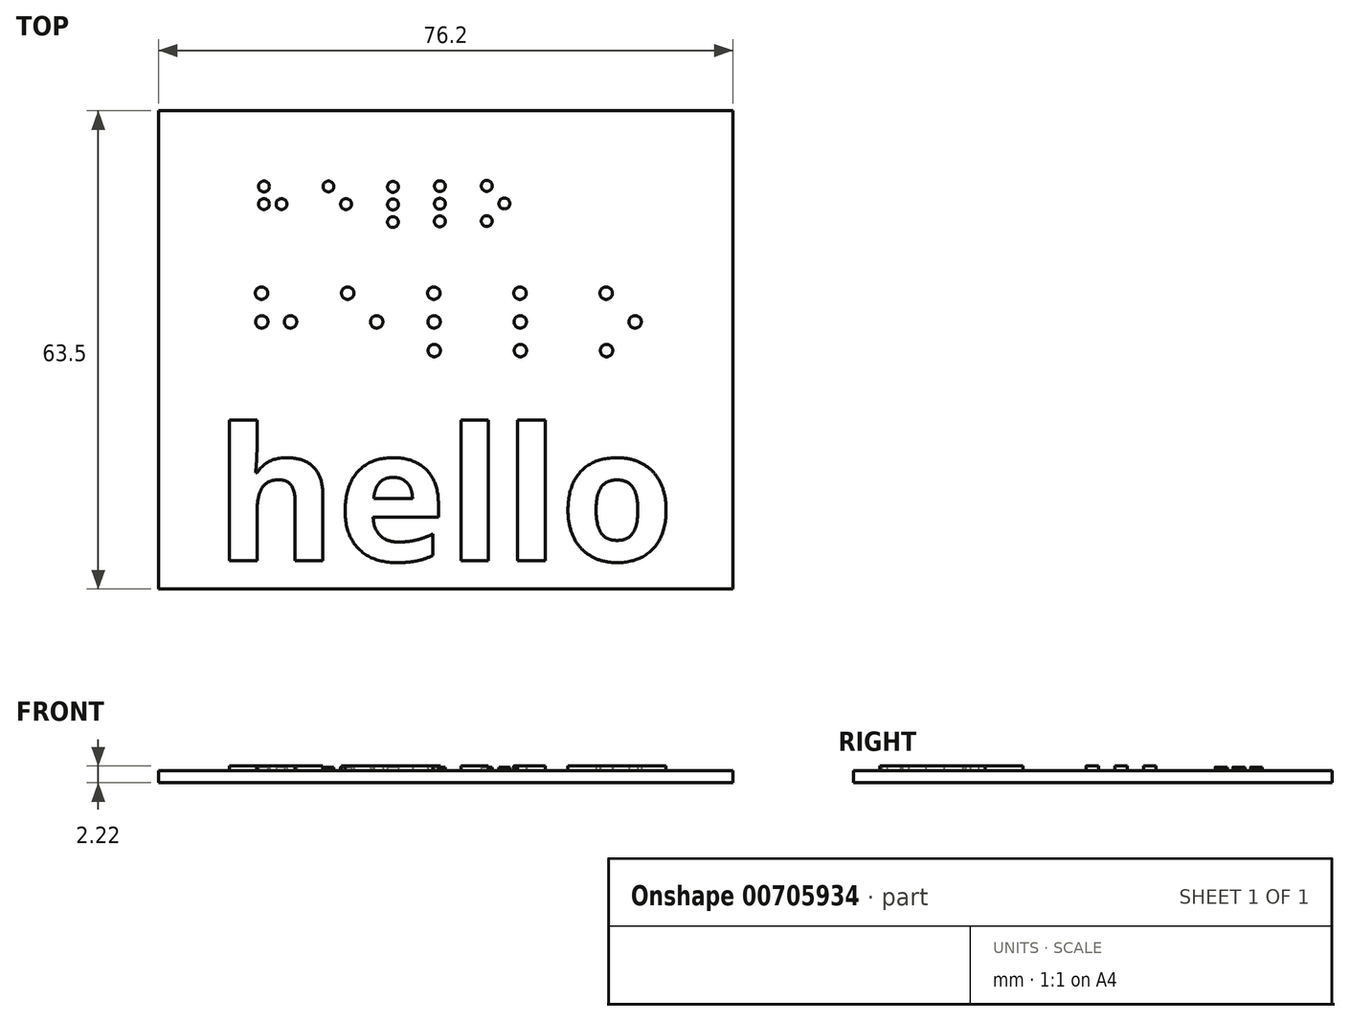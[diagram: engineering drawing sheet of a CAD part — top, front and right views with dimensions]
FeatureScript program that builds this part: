
annotation { "Feature Type Name" : "Feature", "Feature Type Description" : "" }
export const myFeature = defineFeature(function(context is Context, id is Id, definition is map)
    precondition{}
    {
        {
            var Q0;
            Q0=qCreatedBy(makeId("Top.planeOp"),FACE);
            var sketch = newSketch(context, id + "F0", { "sketchPlane" : qUnion([Q0])});
            skLineSegment(sketch, "E0.bottom", {"start": v(2.28, 0) * mm, "end": v(78.48, 0) * mm});
            skLineSegment(sketch, "E0.top", {"start": v(2.28, 63.5) * mm, "end": v(78.48, 63.5) * mm});
            skLineSegment(sketch, "E0.left", {"start": v(2.28, 0) * mm, "end": v(2.28, 63.5) * mm});
            skLineSegment(sketch, "E0.right", {"start": v(78.48, 0) * mm, "end": v(78.48, 63.5) * mm});
            skSolve(sketch);
        }
        {
            var Q0;
            Q0=makeQuery(id+"F0.imprint","IMPRINT",FACE,{"disambiguationData":[TD([[makeQuery(id+"F0.imprint","IMPRINT",EDGE,{"derivedFrom":sQuery(id+"F0.wireOp",EDGE,"E0.bottom")}),1.0]])]});
            extrude(context, id + "F1", {"entities" : qUnion([Q0]), "depth" : 1.59 * mm, "offsetDistance" : 25.4 * mm});
        }
        {
            var Q0;
            Q0=makeQuery(id+"F1.opExtrude","CAP_FACE",FACE,{"disambiguationData":[OSD([sQuery(id+"F0.wireOp",EDGE,"E0.bottom"),sQuery(id+"F0.wireOp",EDGE,"E0.top"),sQuery(id+"F0.wireOp",EDGE,"E0.left"),sQuery(id+"F0.wireOp",EDGE,"E0.right")])],"isStart":false});
            var sketch = newSketch(context, id + "F2", { "sketchPlane" : qUnion([Q0])});
            skCircle(sketch, "E1", {"center": v(16.26, 53.45) * mm, "radius": 0.72 * mm});
            skLineSegment(sketch, "E2.direction1", {"start": v(16.26, 53.45) * mm, "end": v(18.6, 53.45) * mm, "construction": true});
            skCircle(sketch, "E3.1.0.0", {"center": v(16.26, 51.11) * mm, "radius": 0.72 * mm});
            skCircle(sketch, "E3.1.0.1", {"center": v(18.6, 51.11) * mm, "radius": 0.72 * mm});
            skLineSegment(sketch, "E3.direction1", {"start": v(16.26, 53.45) * mm, "end": v(16.26, 51.11) * mm, "construction": true});
            skCircle(sketch, "E4", {"center": v(24.82, 53.45) * mm, "radius": 0.72 * mm});
            skCircle(sketch, "E5.1.0.1", {"center": v(27.15, 51.11) * mm, "radius": 0.72 * mm});
            skCircle(sketch, "E6", {"center": v(33.38, 53.4) * mm, "radius": 0.72 * mm});
            skCircle(sketch, "E7.1.0.0", {"center": v(33.38, 51.06) * mm, "radius": 0.72 * mm});
            skCircle(sketch, "E7.2.0.0", {"center": v(33.37, 48.73) * mm, "radius": 0.72 * mm});
            skCircle(sketch, "E8", {"center": v(39.6, 53.5) * mm, "radius": 0.72 * mm});
            skCircle(sketch, "E9.1.0.0", {"center": v(39.6, 51.16) * mm, "radius": 0.72 * mm});
            skCircle(sketch, "E9.2.0.0", {"center": v(39.6, 48.82) * mm, "radius": 0.72 * mm});
            skCircle(sketch, "E10", {"center": v(45.83, 53.53) * mm, "radius": 0.72 * mm});
            skCircle(sketch, "E11.1.0.1", {"center": v(48.16, 51.2) * mm, "radius": 0.72 * mm});
            skCircle(sketch, "E11.2.0.0", {"center": v(45.82, 48.86) * mm, "radius": 0.72 * mm});
            skPoint(sketch, "E3.2.0.0.center.orphan", {"position": v(16.25, 48.78) * mm});
            skPoint(sketch, "E5.1.0.0.center.orphan", {"position": v(24.82, 51.11) * mm});
            skPoint(sketch, "E5.2.0.0.center.orphan", {"position": v(24.81, 48.78) * mm});
            skPoint(sketch, "E12.1.0.0.center.orphan", {"position": v(27.16, 53.45) * mm});
            skPoint(sketch, "E13.1.0.0.center.orphan", {"position": v(35.72, 53.4) * mm});
            skPoint(sketch, "E7.1.0.1.center.orphan", {"position": v(35.71, 51.06) * mm});
            skPoint(sketch, "E7.2.0.1.center.orphan", {"position": v(35.7, 48.73) * mm});
            skPoint(sketch, "E14.1.0.0.center.orphan", {"position": v(41.94, 53.5) * mm});
            skPoint(sketch, "E9.1.0.1.center.orphan", {"position": v(41.94, 51.16) * mm});
            skPoint(sketch, "E9.2.0.1.center.orphan", {"position": v(41.93, 48.82) * mm});
            skPoint(sketch, "E11.1.0.0.center.orphan", {"position": v(45.82, 51.2) * mm});
            skPoint(sketch, "E11.2.0.1.center.orphan", {"position": v(48.15, 48.86) * mm});
            skPoint(sketch, "E15.1.0.0.center.orphan", {"position": v(48.16, 53.53) * mm});
            skPoint(sketch, "E16.center.orphan", {"position": v(52.05, 53.48) * mm});
            skPoint(sketch, "E17.1.0.0.center.orphan", {"position": v(52.05, 51.14) * mm});
            skPoint(sketch, "E17.1.0.1.center.orphan", {"position": v(54.38, 51.14) * mm});
            skPoint(sketch, "E18.1.0.0.center.orphan", {"position": v(54.39, 53.48) * mm});
            skPoint(sketch, "E17.2.0.0.center.orphan", {"position": v(52.04, 48.8) * mm});
            skPoint(sketch, "E17.2.0.1.center.orphan", {"position": v(54.38, 48.8) * mm});
            skPoint(sketch, "E19.orphan", {"position": v(52.04, 48.05) * mm});
            skPoint(sketch, "E20.start.orphan", {"position": v(27.15, 48.78) * mm});
            skPoint(sketch, "E21.start.orphan", {"position": v(16.25, 48.05) * mm});
            skSolve(sketch);
        }
        {
            var Q0;
            Q0=makeQuery(id+"F2.imprint","IMPRINT",FACE,{"disambiguationData":[TD([[makeQuery(id+"F2.imprint","IMPRINT",EDGE,{"derivedFrom":sQuery(id+"F2.wireOp",EDGE,"E3.1.0.0")}),1.0]])]});
            var Q1;
            Q1=makeQuery(id+"F2.imprint","IMPRINT",FACE,{"disambiguationData":[TD([[makeQuery(id+"F2.imprint","IMPRINT",EDGE,{"derivedFrom":sQuery(id+"F2.wireOp",EDGE,"E3.1.0.1")}),1.0]])]});
            var Q2;
            Q2=makeQuery(id+"F2.imprint","IMPRINT",FACE,{"disambiguationData":[TD([[makeQuery(id+"F2.imprint","IMPRINT",EDGE,{"derivedFrom":sQuery(id+"F2.wireOp",EDGE,"E1")}),1.0]])]});
            var Q3;
            Q3=makeQuery(id+"F2.imprint","IMPRINT",FACE,{"disambiguationData":[TD([[makeQuery(id+"F2.imprint","IMPRINT",EDGE,{"derivedFrom":sQuery(id+"F2.wireOp",EDGE,"E4")}),1.0]])]});
            var Q4;
            Q4=makeQuery(id+"F2.imprint","IMPRINT",FACE,{"disambiguationData":[TD([[makeQuery(id+"F2.imprint","IMPRINT",EDGE,{"derivedFrom":sQuery(id+"F2.wireOp",EDGE,"E5.1.0.1")}),1.0]])]});
            var Q5;
            Q5=makeQuery(id+"F2.imprint","IMPRINT",FACE,{"disambiguationData":[TD([[makeQuery(id+"F2.imprint","IMPRINT",EDGE,{"derivedFrom":sQuery(id+"F2.wireOp",EDGE,"E7.2.0.0")}),1.0]])]});
            var Q6;
            Q6=makeQuery(id+"F2.imprint","IMPRINT",FACE,{"disambiguationData":[TD([[makeQuery(id+"F2.imprint","IMPRINT",EDGE,{"derivedFrom":sQuery(id+"F2.wireOp",EDGE,"E7.1.0.0")}),1.0]])]});
            var Q7;
            Q7=makeQuery(id+"F2.imprint","IMPRINT",FACE,{"disambiguationData":[TD([[makeQuery(id+"F2.imprint","IMPRINT",EDGE,{"derivedFrom":sQuery(id+"F2.wireOp",EDGE,"E6")}),1.0]])]});
            var Q8;
            Q8=makeQuery(id+"F2.imprint","IMPRINT",FACE,{"disambiguationData":[TD([[makeQuery(id+"F2.imprint","IMPRINT",EDGE,{"derivedFrom":sQuery(id+"F2.wireOp",EDGE,"E9.2.0.0")}),1.0]])]});
            var Q9;
            Q9=makeQuery(id+"F2.imprint","IMPRINT",FACE,{"disambiguationData":[TD([[makeQuery(id+"F2.imprint","IMPRINT",EDGE,{"derivedFrom":sQuery(id+"F2.wireOp",EDGE,"E9.1.0.0")}),1.0]])]});
            var Q10;
            Q10=makeQuery(id+"F2.imprint","IMPRINT",FACE,{"disambiguationData":[TD([[makeQuery(id+"F2.imprint","IMPRINT",EDGE,{"derivedFrom":sQuery(id+"F2.wireOp",EDGE,"E8")}),1.0]])]});
            var Q11;
            Q11=makeQuery(id+"F2.imprint","IMPRINT",FACE,{"disambiguationData":[TD([[makeQuery(id+"F2.imprint","IMPRINT",EDGE,{"derivedFrom":sQuery(id+"F2.wireOp",EDGE,"E11.2.0.0")}),1.0]])]});
            var Q12;
            Q12=makeQuery(id+"F2.imprint","IMPRINT",FACE,{"disambiguationData":[TD([[makeQuery(id+"F2.imprint","IMPRINT",EDGE,{"derivedFrom":sQuery(id+"F2.wireOp",EDGE,"E11.1.0.1")}),1.0]])]});
            var Q13;
            Q13=makeQuery(id+"F2.imprint","IMPRINT",FACE,{"disambiguationData":[TD([[makeQuery(id+"F2.imprint","IMPRINT",EDGE,{"derivedFrom":sQuery(id+"F2.wireOp",EDGE,"E10")}),1.0]])]});
            extrude(context, id + "F3", {"entities" : qUnion([Q0, Q1, Q2, Q3, Q4, Q5, Q6, Q7, Q8, Q9, Q10, Q11, Q12, Q13]), "operationType" : NewBodyOperationType.ADD, "depth" : 0.48 * mm, "offsetDistance" : 25.4 * mm});
        }
        {
            var Q0;
            Q0=makeQuery(id+"F1.opExtrude","CAP_FACE",FACE,{"disambiguationData":[OSD([sQuery(id+"F0.wireOp",EDGE,"E0.bottom"),sQuery(id+"F0.wireOp",EDGE,"E0.top"),sQuery(id+"F0.wireOp",EDGE,"E0.left"),sQuery(id+"F0.wireOp",EDGE,"E0.right")])],"isStart":false});
            var sketch = newSketch(context, id + "F4", { "sketchPlane" : qUnion([Q0])});
            skCircle(sketch, "E22", {"center": v(15.94, 39.3) * mm, "radius": 0.83 * mm});
            skCircle(sketch, "E23.1.0.0", {"center": v(15.97, 35.48) * mm, "radius": 0.83 * mm});
            skCircle(sketch, "E23.1.0.1", {"center": v(19.78, 35.48) * mm, "radius": 0.83 * mm});
            skCircle(sketch, "E24", {"center": v(27.37, 39.3) * mm, "radius": 0.83 * mm});
            skCircle(sketch, "E25.1.0.1", {"center": v(31.2, 35.48) * mm, "radius": 0.83 * mm});
            skCircle(sketch, "E26", {"center": v(38.8, 39.3) * mm, "radius": 0.83 * mm});
            skCircle(sketch, "E27.1.0.0", {"center": v(38.83, 35.48) * mm, "radius": 0.83 * mm});
            skCircle(sketch, "E27.2.0.0", {"center": v(38.86, 31.67) * mm, "radius": 0.83 * mm});
            skCircle(sketch, "E28", {"center": v(50.23, 39.3) * mm, "radius": 0.83 * mm});
            skCircle(sketch, "E29.1.0.0", {"center": v(50.26, 35.48) * mm, "radius": 0.83 * mm});
            skCircle(sketch, "E29.2.0.0", {"center": v(50.29, 31.67) * mm, "radius": 0.83 * mm});
            skCircle(sketch, "E30", {"center": v(61.66, 39.3) * mm, "radius": 0.83 * mm});
            skCircle(sketch, "E31.1.0.1", {"center": v(65.5, 35.48) * mm, "radius": 0.83 * mm});
            skCircle(sketch, "E31.2.0.0", {"center": v(61.72, 31.67) * mm, "radius": 0.83 * mm});
            skPoint(sketch, "E23.2.0.0.center.orphan", {"position": v(16, 31.67) * mm});
            skPoint(sketch, "E23.2.0.1.center.orphan", {"position": v(19.8, 31.67) * mm});
            skPoint(sketch, "E25.2.0.0.center.orphan", {"position": v(27.43, 31.67) * mm});
            skPoint(sketch, "E25.2.0.1.center.orphan", {"position": v(31.24, 31.67) * mm});
            skSolve(sketch);
        }
        {
            var Q0;
            Q0 = qSketchRegion(id + "F4", true);
            extrude(context, id + "F5", {"entities" : qUnion([Q0]), "operationType" : NewBodyOperationType.ADD, "depth" : 0.64 * mm, "offsetDistance" : 25.4 * mm});
        }
        {
            var Q0;
            Q0=makeQuery(id+"F1.opExtrude","CAP_FACE",FACE,{"disambiguationData":[OSD([sQuery(id+"F0.wireOp",EDGE,"E0.bottom"),sQuery(id+"F0.wireOp",EDGE,"E0.top"),sQuery(id+"F0.wireOp",EDGE,"E0.left"),sQuery(id+"F0.wireOp",EDGE,"E0.right")])],"isStart":false});
            var sketch = newSketch(context, id + "F6", { "sketchPlane" : qUnion([Q0])});
            skText(sketch, "E32", { "text": "hello", "fontName": "OpenSans-Bold.ttf"});
            const initialGuessF6  = {"E32": [0.00975, 0.00376, 1, 0, 0.01772]};
            skSetInitialGuess(sketch, initialGuessF6);
            skSolve(sketch);
        }
        {
            var Q0;
            Q0=makeQuery(id+"F6.imprint","IMPRINT",FACE,{"disambiguationData":[TD([[makeQuery(id+"F6.imprint","IMPRINT",EDGE,{"derivedFrom":sQuery(id+"F6.wireOp",EDGE,"E32.sketch_text.stroke-0")}),-1.0]])]});
            var Q1;
            Q1=makeQuery(id+"F6.imprint","IMPRINT",FACE,{"disambiguationData":[TD([[makeQuery(id+"F6.imprint","IMPRINT",EDGE,{"derivedFrom":sQuery(id+"F6.wireOp",EDGE,"E32.sketch_text.stroke-17")}),-1.0]])]});
            var Q2;
            Q2=makeQuery(id+"F6.imprint","IMPRINT",FACE,{"disambiguationData":[TD([[makeQuery(id+"F6.imprint","IMPRINT",EDGE,{"derivedFrom":sQuery(id+"F6.wireOp",EDGE,"E32.sketch_text.stroke-37")}),-1.0]])]});
            var Q3;
            Q3=makeQuery(id+"F6.imprint","IMPRINT",FACE,{"disambiguationData":[TD([[makeQuery(id+"F6.imprint","IMPRINT",EDGE,{"derivedFrom":sQuery(id+"F6.wireOp",EDGE,"E32.sketch_text.stroke-41")}),-1.0]])]});
            var Q4;
            Q4=makeQuery(id+"F6.imprint","IMPRINT",FACE,{"disambiguationData":[TD([[makeQuery(id+"F6.imprint","IMPRINT",EDGE,{"derivedFrom":sQuery(id+"F6.wireOp",EDGE,"E32.sketch_text.stroke-45")}),-1.0]])]});
            extrude(context, id + "F7", {"entities" : qUnion([Q0, Q1, Q2, Q3, Q4]), "operationType" : NewBodyOperationType.ADD, "depth" : 0.64 * mm, "offsetDistance" : 25.4 * mm});
        }
    });
